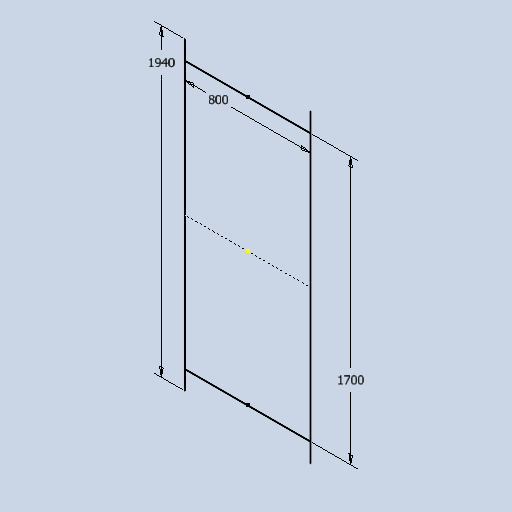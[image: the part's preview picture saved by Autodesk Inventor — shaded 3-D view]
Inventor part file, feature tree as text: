
AUTODESK INVENTOR PART (.ipt)
format: ipt  version: 2025 (Build 290162010, 162A)  size: 253,440 bytes
history: native  units: mm
features: sketch x1
ambient origin geometry x8: Origin, YZ Plane, XZ Plane, XY Plane, X Axis, Y Axis, Z Axis, Center Point
feature tree (1):
  sketch  "Sketch1"  dims[d0=1940.0mm d1=800.0mm d2=1700.0mm]
